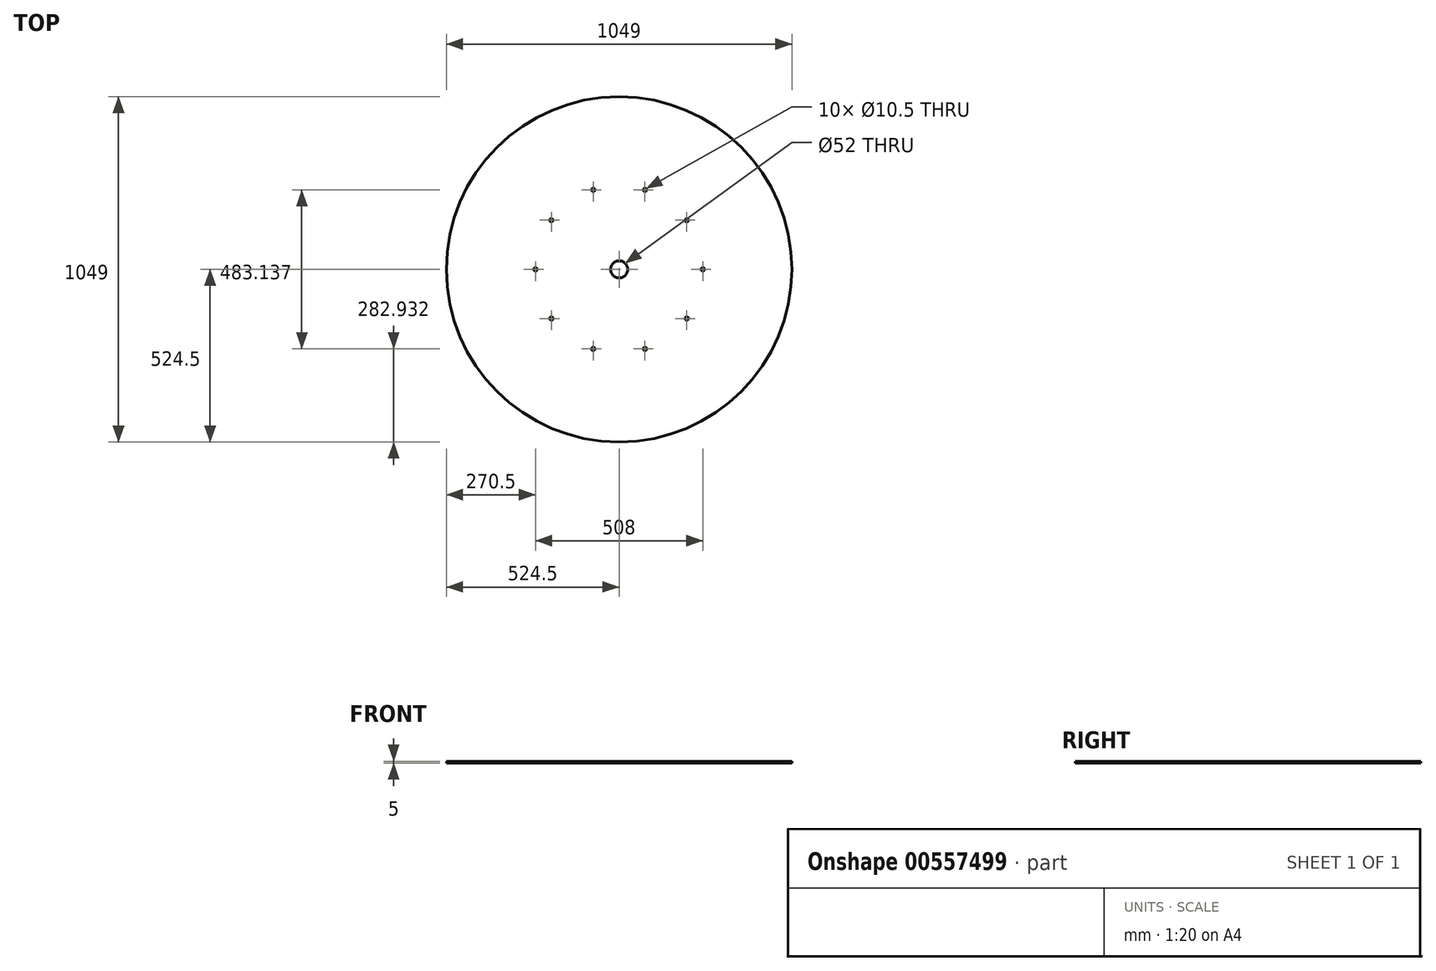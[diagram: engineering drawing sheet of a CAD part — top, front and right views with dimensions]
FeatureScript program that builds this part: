
annotation { "Feature Type Name" : "Feature", "Feature Type Description" : "" }
export const myFeature = defineFeature(function(context is Context, id is Id, definition is map)
    precondition{}
    {
        {
            var Q0;
            Q0=qCreatedBy(makeId("Top.planeOp"),FACE);
            var sketch = newSketch(context, id + "F0", { "sketchPlane" : qUnion([Q0])});
            skCircle(sketch, "E0", {"center": v(0, 0) * mm, "radius": 524.5 * mm});
            skCircle(sketch, "E1", {"center": v(0, 0) * mm, "radius": 26 * mm});
            skCircle(sketch, "E2", {"center": v(0, 0) * mm, "radius": 254 * mm, "construction": true});
            skCircle(sketch, "E3", {"center": v(254, 0) * mm, "radius": 5.25 * mm});
            skCircle(sketch, "E4.1.0", {"center": v(205.5, 149.3) * mm, "radius": 5.25 * mm});
            skCircle(sketch, "E4.2.0", {"center": v(78.5, 241.57) * mm, "radius": 5.25 * mm});
            skCircle(sketch, "E4.3.0", {"center": v(-78.5, 241.57) * mm, "radius": 5.25 * mm});
            skCircle(sketch, "E4.4.0", {"center": v(-205.5, 149.3) * mm, "radius": 5.25 * mm});
            skCircle(sketch, "E4.5.0", {"center": v(-254, 0) * mm, "radius": 5.25 * mm});
            skCircle(sketch, "E4.6.0", {"center": v(-205.5, -149.3) * mm, "radius": 5.25 * mm});
            skCircle(sketch, "E4.7.0", {"center": v(-78.5, -241.57) * mm, "radius": 5.25 * mm});
            skCircle(sketch, "E4.8.0", {"center": v(78.5, -241.57) * mm, "radius": 5.25 * mm});
            skCircle(sketch, "E4.9.0", {"center": v(205.5, -149.3) * mm, "radius": 5.25 * mm});
            skSolve(sketch);
        }
        {
            var Q0;
            Q0=makeQuery(id+"F0.imprint","IMPRINT",FACE,{"disambiguationData":[TD([[makeQuery(id+"F0.imprint","IMPRINT",EDGE,{"derivedFrom":sQuery(id+"F0.wireOp",EDGE,"E0")}),1.0]])]});
            extrude(context, id + "F1", {"entities" : qUnion([Q0]), "depth" : 5 * mm, "offsetDistance" : 25 * mm});
        }
    });
